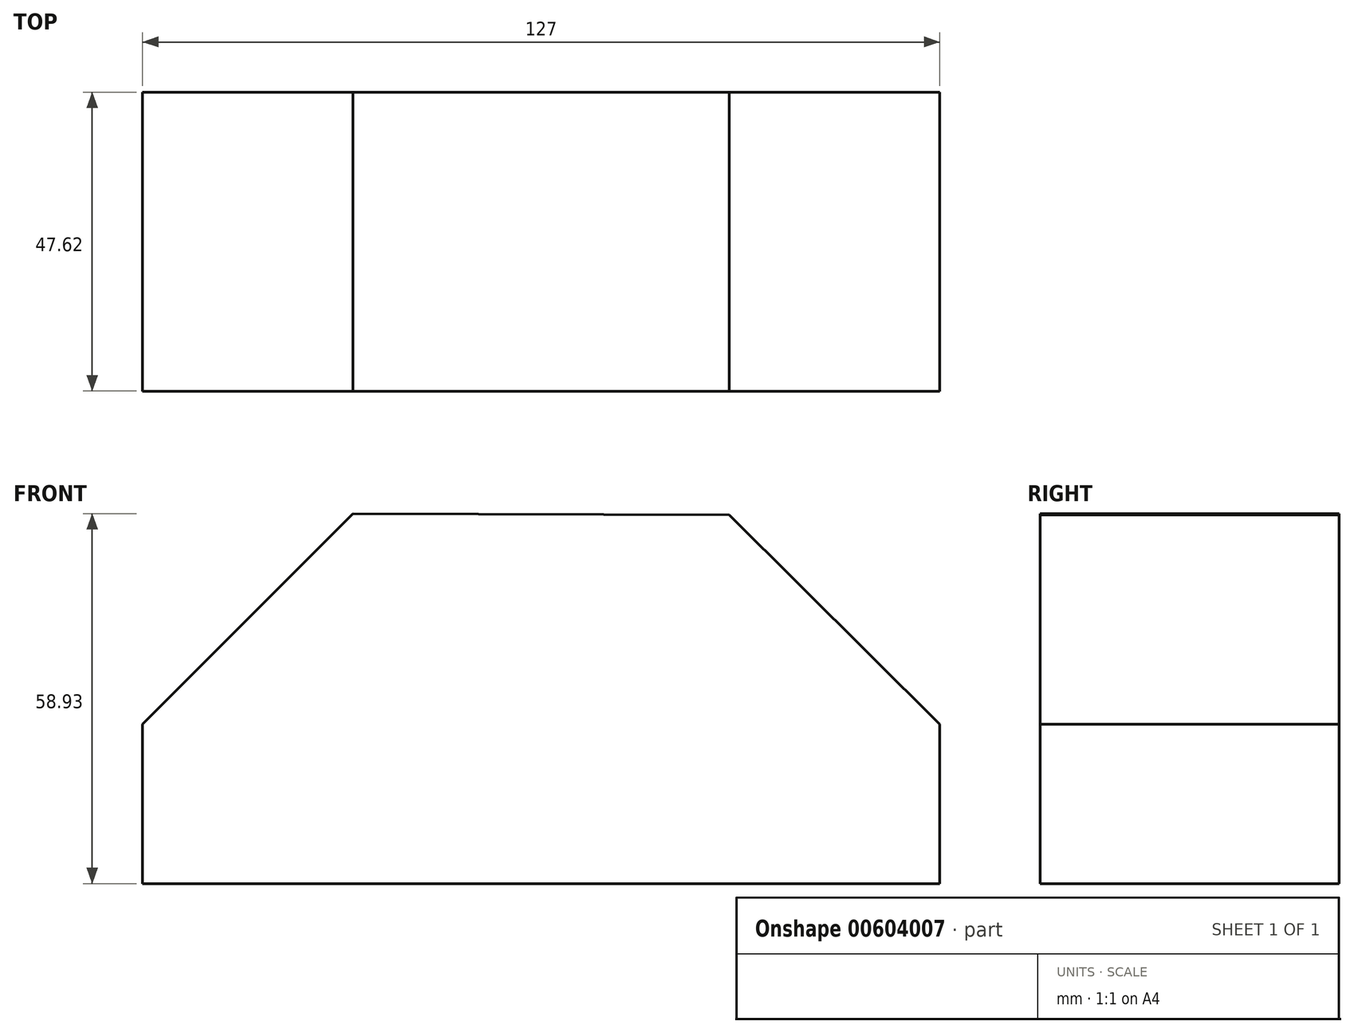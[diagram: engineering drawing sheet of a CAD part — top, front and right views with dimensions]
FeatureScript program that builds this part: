
annotation { "Feature Type Name" : "Feature", "Feature Type Description" : "" }
export const myFeature = defineFeature(function(context is Context, id is Id, definition is map)
    precondition{}
    {
        {
            var Q0;
            Q0=qCreatedBy(makeId("Front.planeOp"),FACE);
            var sketch = newSketch(context, id + "F0", { "sketchPlane" : qUnion([Q0])});
            skLineSegment(sketch, "E0", {"start": v(0, 0) * mm, "end": v(-63.5, 0) * mm});
            skLineSegment(sketch, "E1", {"start": v(0, 0) * mm, "end": v(63.5, 0) * mm});
            skLineSegment(sketch, "E2", {"start": v(63.5, 0) * mm, "end": v(63.5, 25.4) * mm});
            skPoint(sketch, "E3.end.orphan", {"position": v(107.04, 0) * mm});
            skLineSegment(sketch, "E4", {"start": v(63.5, 58.74) * mm, "end": v(29.97, 58.74) * mm, "construction": true});
            skLineSegment(sketch, "E5", {"start": v(63.5, 25.4) * mm, "end": v(29.97, 58.74) * mm});
            skLineSegment(sketch, "E6", {"start": v(-63.5, 0) * mm, "end": v(-63.5, 25.4) * mm});
            skLineSegment(sketch, "E7", {"start": v(-63.5, 25.4) * mm, "end": v(-63.5, 58.93) * mm, "construction": true});
            skLineSegment(sketch, "E8", {"start": v(-63.5, 58.93) * mm, "end": v(-29.97, 58.93) * mm, "construction": true});
            skLineSegment(sketch, "E9", {"start": v(-63.5, 25.4) * mm, "end": v(-29.97, 58.93) * mm});
            skLineSegment(sketch, "E10", {"start": v(-29.97, 58.93) * mm, "end": v(29.97, 58.74) * mm});
            skLineSegment(sketch, "E11", {"start": v(63.5, 25.4) * mm, "end": v(63.5, 58.74) * mm});
            skSolve(sketch);
        }
        {
            var Q0;
            Q0=makeQuery(id+"F0.imprint","IMPRINT",FACE,{"disambiguationData":[TD([[makeQuery(id+"F0.imprint","IMPRINT",EDGE,{"derivedFrom":sQuery(id+"F0.wireOp",EDGE,"E0")}),-1.0]])]});
            extrude(context, id + "F1", {"entities" : qUnion([Q0]), "depth" : 47.62 * mm, "offsetDistance" : 25.4 * mm});
        }
    });
